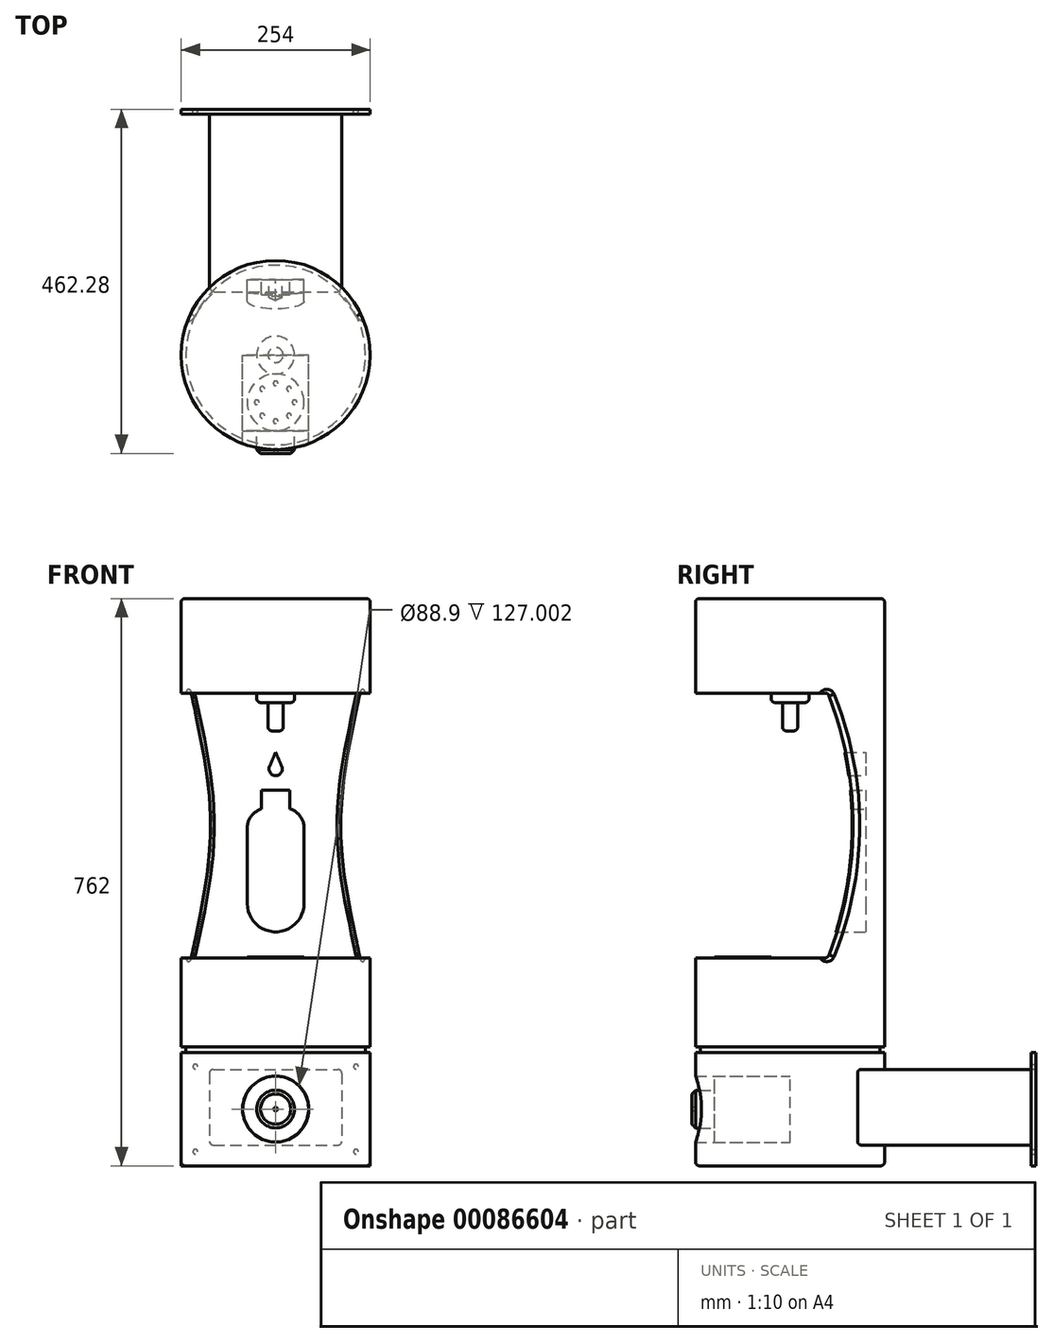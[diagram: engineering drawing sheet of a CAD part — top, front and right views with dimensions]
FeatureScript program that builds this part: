
annotation { "Feature Type Name" : "Feature", "Feature Type Description" : "" }
export const myFeature = defineFeature(function(context is Context, id is Id, definition is map)
    precondition{}
    {
        {
            var Q0;
            Q0=qCreatedBy(makeId("Top.planeOp"),FACE);
            var sketch = newSketch(context, id + "F0", { "sketchPlane" : qUnion([Q0])});
            skCircle(sketch, "E0", {"center": v(0, 0) * mm, "radius": 127 * mm});
            skSolve(sketch);
        }
        {
            var Q0;
            Q0=qCreatedBy(makeId("Front.planeOp"),FACE);
            cPlane(context, id + "F1", {"entities" : qUnion([Q0]), "cplaneType" : CPlaneType.OFFSET, "offset" : 101.6 * mm, "oppositeDirection" : true, "width" : 152.4 * mm, "height" : 152.4 * mm});
        }
        {
            var Q0;
            Q0 = qSketchRegion(id + "F0", true);
            extrude(context, id + "F2", {"entities" : qUnion([Q0]), "depth" : 762 * mm});
        }
        {
            var Q0;
            Q0=qCreatedBy(makeId("Right.planeOp"),FACE);
            var sketch = newSketch(context, id + "F3", { "sketchPlane" : qUnion([Q0])});
            skLineSegment(sketch, "E1.bottom", {"start": v(-152.4, 635) * mm, "end": v(50.8, 635) * mm});
            skLineSegment(sketch, "E1.top", {"start": v(-152.4, 279.4) * mm, "end": v(50.8, 279.4) * mm});
            skLineSegment(sketch, "E1.left", {"start": v(-152.4, 635) * mm, "end": v(-152.4, 279.4) * mm});
            skArc(sketch, "E2", {"start": v(50.8, 279.4) * mm, "mid": v(84.75, 457.2) * mm, "end": v(50.8, 635) * mm});
            skSolve(sketch);
        }
        {
            var Q0;
            Q0=qCreatedBy(id+"F1.planeOp",FACE);
            var sketch = newSketch(context, id + "F4", { "sketchPlane" : qUnion([Q0])});
            skLineSegment(sketch, "E3", {"start": v(0, 504.76) * mm, "end": v(-19.05, 504.76) * mm});
            skLineSegment(sketch, "E4", {"start": v(-19.05, 504.76) * mm, "end": v(-19.05, 479.36) * mm});
            skLineSegment(sketch, "E5", {"start": v(-38.1, 453.96) * mm, "end": v(-38.1, 352.36) * mm});
            skLineSegment(sketch, "E6", {"start": v(0, 96.81) * mm, "end": v(0, 607) * mm, "construction": true});
            skArc(sketch, "E7", {"start": v(-38.1, 453.96) * mm, "mid": v(-32.8, 469.83) * mm, "end": v(-19.05, 479.36) * mm});
            skArc(sketch, "E8", {"start": v(-38.1, 352.36) * mm, "mid": v(-26.94, 325.42) * mm, "end": v(0, 314.26) * mm});
            skLineSegment(sketch, "E9.MirrorCS", {"start": v(19.05, 504.76) * mm, "end": v(19.05, 479.36) * mm});
            skArc(sketch, "E10.MirrorCS", {"start": v(38.1, 352.36) * mm, "mid": v(26.94, 325.42) * mm, "end": v(0, 314.26) * mm});
            skLineSegment(sketch, "E11.MirrorCS", {"start": v(38.1, 453.96) * mm, "end": v(38.1, 352.36) * mm});
            skArc(sketch, "E12.MirrorCS", {"start": v(38.1, 453.96) * mm, "mid": v(32.8, 469.83) * mm, "end": v(19.05, 479.36) * mm});
            skLineSegment(sketch, "E13.MirrorCS", {"start": v(0, 504.76) * mm, "end": v(19.05, 504.76) * mm});
            skLineSegment(sketch, "E14", {"start": v(0, 555.56) * mm, "end": v(-8.17, 536.5) * mm});
            skArc(sketch, "E15", {"start": v(-8.17, 536.5) * mm, "mid": v(-7.42, 528.11) * mm, "end": v(0, 524.11) * mm});
            skArc(sketch, "E16.MirrorCS", {"start": v(8.17, 536.5) * mm, "mid": v(7.42, 528.11) * mm, "end": v(0, 524.11) * mm});
            skLineSegment(sketch, "E17.MirrorCS", {"start": v(0, 555.56) * mm, "end": v(8.17, 536.5) * mm});
            skSolve(sketch);
        }
        {
            var Q0;
            Q0 = qSketchRegion(id + "F3", true);
            extrude(context, id + "F5", {"entities" : qUnion([Q0]), "operationType" : NewBodyOperationType.REMOVE, "oppositeDirection" : true, "depth" : 152.4 * mm, "hasSecondDirection" : true, "secondDirectionOppositeDirection" : false, "secondDirectionDepth" : 152.4 * mm});
        }
        {
            var Q0;
            Q0=qCreatedBy(makeId("Front.planeOp"),FACE);
            var sketch = newSketch(context, id + "F6", { "sketchPlane" : qUnion([Q0])});
            skLineSegment(sketch, "E18.bottom", {"start": v(146.05, 160.02) * mm, "end": v(120.65, 160.02) * mm});
            skLineSegment(sketch, "E18.top", {"start": v(146.05, 152.4) * mm, "end": v(120.65, 152.4) * mm});
            skLineSegment(sketch, "E18.left", {"start": v(146.05, 160.02) * mm, "end": v(146.05, 152.4) * mm});
            skLineSegment(sketch, "E18.right", {"start": v(120.65, 160.02) * mm, "end": v(120.65, 152.4) * mm});
            skLineSegment(sketch, "E19", {"start": v(0, 0) * mm, "end": v(0, 233.9) * mm, "construction": true});
            skSolve(sketch);
        }
        {
            var Q0;
            Q0 = qSketchRegion(id + "F6", true);
            var Q1;
            Q1=sQuery(id+"F6.wireOp",EDGE,"E19");
            revolve(context, id + "F7", {"operationType" : NewBodyOperationType.REMOVE, "entities" : qUnion([Q0]), "axis" : qUnion([Q1]), "revolveType" : RevolveType.FULL, "oppositeDirection" : true});
        }
        {
            var Q0;
            Q0=qCreatedBy(makeId("Front.planeOp"),FACE);
            var sketch = newSketch(context, id + "F8", { "sketchPlane" : qUnion([Q0])});
            skLineSegment(sketch, "E20", {"start": v(0, 635) * mm, "end": v(0, 584.2) * mm});
            skLineSegment(sketch, "E21", {"start": v(0, 584.2) * mm, "end": v(10.16, 584.2) * mm});
            skLineSegment(sketch, "E22", {"start": v(10.16, 584.2) * mm, "end": v(10.16, 622.3) * mm});
            skLineSegment(sketch, "E23", {"start": v(10.16, 622.3) * mm, "end": v(25.4, 622.3) * mm});
            skLineSegment(sketch, "E24", {"start": v(25.4, 622.3) * mm, "end": v(25.4, 635) * mm});
            skLineSegment(sketch, "E25", {"start": v(0, 635) * mm, "end": v(25.4, 635) * mm});
            skLineSegment(sketch, "E26", {"start": v(0, 635) * mm, "end": v(0, 489.38) * mm, "construction": true});
            skSolve(sketch);
        }
        {
            var Q0;
            Q0 = qSketchRegion(id + "F8", true);
            var Q1;
            Q1=sQuery(id+"F8.wireOp",EDGE,"E26");
            revolve(context, id + "F9", {"entities" : qUnion([Q0]), "axis" : qUnion([Q1]), "revolveType" : RevolveType.FULL});
        }
        {
            var Q0;
            Q0=makeQuery(id+"F5.boolean.opBoolean","COPY",FACE,{"derivedFrom":makeQuery(id+"F5.opExtrude","SWEPT_FACE",FACE,{"disambiguationData":[OSD([sQuery(id+"F3.wireOp",EDGE,"E1.top")])]})});
            var sketch = newSketch(context, id + "F10", { "sketchPlane" : qUnion([Q0])});
            skCircle(sketch, "E27", {"center": v(0, -38.1) * mm, "radius": 3.18 * mm});
            skCircle(sketch, "E28.1.0", {"center": v(-17.96, -45.54) * mm, "radius": 3.18 * mm});
            skCircle(sketch, "E28.2.0", {"center": v(-25.4, -63.5) * mm, "radius": 3.18 * mm});
            skCircle(sketch, "E28.3.0", {"center": v(-17.96, -81.46) * mm, "radius": 3.18 * mm});
            skCircle(sketch, "E28.4.0", {"center": v(0, -88.9) * mm, "radius": 3.18 * mm});
            skCircle(sketch, "E28.5.0", {"center": v(17.96, -81.46) * mm, "radius": 3.18 * mm});
            skCircle(sketch, "E28.6.0", {"center": v(25.4, -63.5) * mm, "radius": 3.18 * mm});
            skCircle(sketch, "E28.7.0", {"center": v(17.96, -45.54) * mm, "radius": 3.18 * mm});
            skPoint(sketch, "E28.center", {"position": v(0, -63.5) * mm});
            skCircle(sketch, "E29.0", {"center": v(0, -63.5) * mm, "radius": 38.1 * mm});
            skSolve(sketch);
        }
        {
            var Q0;
            Q0 = qSketchRegion(id + "F10", true);
            extrude(context, id + "F11", {"entities" : qUnion([Q0]), "depth" : 1.27 * mm});
        }
        {
            var Q0;
            Q0=makeQuery(id+"F9.opRevolve","SWEPT_EDGE",EDGE,{"disambiguationData":[OSD([sQuery(id+"F8.wireOp",EDGE,"E23"),sQuery(id+"F8.wireOp",EDGE,"E24")])]});
            var Q1;
            Q1=makeQuery(id+"F9.opRevolve","SWEPT_EDGE",EDGE,{"disambiguationData":[OSD([sQuery(id+"F8.wireOp",EDGE,"E21"),sQuery(id+"F8.wireOp",EDGE,"E22")])]});
            fillet(context, id + "F12", {"entities" : qUnion([Q0, Q1]), "radius" : 5.08 * mm, "tangentPropagation" : true, "allowEdgeOverflow" : false});
        }
        {
            var Q0;
            Q0=makeQuery(id+"F5.boolean.opBoolean","COPY",FACE,{"derivedFrom":makeQuery(id+"F5.opExtrude","SWEPT_FACE",FACE,{"disambiguationData":[OSD([sQuery(id+"F3.wireOp",EDGE,"E2")])]})});
            var Q1;
            Q1=makeQuery(id+"F2.opExtrude","CAP_FACE",FACE,{"disambiguationData":[OSD([sQuery(id+"F0.wireOp",EDGE,"E0")])],"isStart":false});
            var Q2;
            Q2=makeQuery(id+"F2.opExtrude","CAP_FACE",FACE,{"disambiguationData":[OSD([sQuery(id+"F0.wireOp",EDGE,"E0")])],"isStart":true});
            fillet(context, id + "F13", {"entities" : qUnion([Q0, Q1, Q2]), "radius" : 5.08 * mm, "tangentPropagation" : true, "allowEdgeOverflow" : false});
        }
        {
            var Q0;
            Q0=qCreatedBy(makeId("Front.planeOp"),FACE);
            var sketch = newSketch(context, id + "F14", { "sketchPlane" : qUnion([Q0])});
            skLineSegment(sketch, "E30.bottom", {"start": v(-88.9, 129.54) * mm, "end": v(88.9, 129.54) * mm});
            skLineSegment(sketch, "E30.top", {"start": v(-88.9, 27.94) * mm, "end": v(88.9, 27.94) * mm});
            skLineSegment(sketch, "E30.left", {"start": v(-88.9, 129.54) * mm, "end": v(-88.9, 27.94) * mm});
            skLineSegment(sketch, "E30.right", {"start": v(88.9, 129.54) * mm, "end": v(88.9, 27.94) * mm});
            skLineSegment(sketch, "E31", {"start": v(-88.9, 78.74) * mm, "end": v(88.9, 78.74) * mm, "construction": true});
            skLineSegment(sketch, "E32", {"start": v(0, 0) * mm, "end": v(0, 109.7) * mm, "construction": true});
            skSolve(sketch);
        }
        {
            var Q0;
            Q0 = qSketchRegion(id + "F14", true);
            extrude(context, id + "F15", {"entities" : qUnion([Q0]), "operationType" : NewBodyOperationType.ADD, "oppositeDirection" : true, "depth" : 330.2 * mm});
        }
        {
            var Q0;
            Q0=makeQuery(id+"F15.opExtrude","CAP_FACE",FACE,{"disambiguationData":[OSD([sQuery(id+"F14.wireOp",EDGE,"E30.bottom"),sQuery(id+"F14.wireOp",EDGE,"E30.top"),sQuery(id+"F14.wireOp",EDGE,"E30.left"),sQuery(id+"F14.wireOp",EDGE,"E30.right")])],"isStart":false});
            var sketch = newSketch(context, id + "F16", { "sketchPlane" : qUnion([Q0])});
            skLineSegment(sketch, "E33.bottom", {"start": v(-127, 152.4) * mm, "end": v(127, 152.4) * mm});
            skLineSegment(sketch, "E33.top", {"start": v(-127, 0) * mm, "end": v(127, 0) * mm});
            skLineSegment(sketch, "E33.left", {"start": v(-127, 152.4) * mm, "end": v(-127, 0) * mm});
            skLineSegment(sketch, "E33.right", {"start": v(127, 152.4) * mm, "end": v(127, 0) * mm});
            skLineSegment(sketch, "E34", {"start": v(0, 0) * mm, "end": v(0, 100.7) * mm, "construction": true});
            skCircle(sketch, "E35", {"center": v(-107.95, 133.35) * mm, "radius": 3.18 * mm});
            skCircle(sketch, "E36", {"center": v(107.95, 133.35) * mm, "radius": 3.18 * mm});
            skCircle(sketch, "E37", {"center": v(107.95, 19.05) * mm, "radius": 3.18 * mm});
            skCircle(sketch, "E38", {"center": v(-107.95, 19.05) * mm, "radius": 3.18 * mm});
            skSolve(sketch);
        }
        {
            var Q0;
            Q0 = qSketchRegion(id + "F16", true);
            extrude(context, id + "F17", {"entities" : qUnion([Q0]), "operationType" : NewBodyOperationType.ADD, "oppositeDirection" : true, "depth" : 6.35 * mm});
        }
        {
            var Q0;
            Q0 = qSketchRegion(id + "F4", true);
            extrude(context, id + "F18", {"entities" : qUnion([Q0]), "depth" : 50.8 * mm});
        }
        {
            var Q0;
            Q0=qCreatedBy(makeId("Right.planeOp"),FACE);
            var sketch = newSketch(context, id + "F19", { "sketchPlane" : qUnion([Q0])});
            skArc(sketch, "E39.0", {"start": v(52.07, 282.64) * mm, "mid": v(84.75, 457.2) * mm, "end": v(52.07, 631.76) * mm});
            skArc(sketch, "E40.0", {"start": v(59.53, 307.27) * mm, "mid": v(82.87, 433.1) * mm, "end": v(72.23, 560.64) * mm});
            skLineSegment(sketch, "E41", {"start": v(72.23, 560.64) * mm, "end": v(34.13, 560.64) * mm});
            skLineSegment(sketch, "E42", {"start": v(34.13, 560.64) * mm, "end": v(34.13, 307.27) * mm});
            skLineSegment(sketch, "E43", {"start": v(34.13, 307.27) * mm, "end": v(59.53, 307.27) * mm});
            skSolve(sketch);
        }
        {
            var Q0;
            Q0 = qSketchRegion(id + "F19", true);
            extrude(context, id + "F20", {"entities" : qUnion([Q0]), "operationType" : NewBodyOperationType.REMOVE, "oppositeDirection" : true, "depth" : 101.6 * mm, "hasSecondDirection" : true, "secondDirectionOppositeDirection" : false, "secondDirectionDepth" : 101.6 * mm});
        }
        {
            var Q0;
            Q0=makeQuery(id+"F15.opExtrude","SWEPT_EDGE",EDGE,{"disambiguationData":[OSD([sQuery(id+"F14.wireOp",EDGE,"E30.bottom"),sQuery(id+"F14.wireOp",EDGE,"E30.right")])]});
            var Q1;
            Q1=makeQuery(id+"F15.opExtrude","SWEPT_EDGE",EDGE,{"disambiguationData":[OSD([sQuery(id+"F14.wireOp",EDGE,"E30.top"),sQuery(id+"F14.wireOp",EDGE,"E30.right")])]});
            var Q2;
            Q2=makeQuery(id+"F15.opExtrude","SWEPT_EDGE",EDGE,{"disambiguationData":[OSD([sQuery(id+"F14.wireOp",EDGE,"E30.top"),sQuery(id+"F14.wireOp",EDGE,"E30.left")])]});
            var Q3;
            Q3=makeQuery(id+"F15.opExtrude","SWEPT_EDGE",EDGE,{"disambiguationData":[OSD([sQuery(id+"F14.wireOp",EDGE,"E30.bottom"),sQuery(id+"F14.wireOp",EDGE,"E30.left")])]});
            fillet(context, id + "F21", {"entities" : qUnion([Q0, Q1, Q2, Q3]), "radius" : 5.08 * mm, "tangentPropagation" : true, "allowEdgeOverflow" : false});
        }
        {
            var Q0;
            Q0=qCreatedBy(makeId("Front.planeOp"),FACE);
            var sketch = newSketch(context, id + "F22", { "sketchPlane" : qUnion([Q0])});
            skCircle(sketch, "E44", {"center": v(0, 76.2) * mm, "radius": 44.45 * mm});
            skSolve(sketch);
        }
        {
            var Q0;
            Q0 = qSketchRegion(id + "F22", true);
            extrude(context, id + "F23", {"entities" : qUnion([Q0]), "operationType" : NewBodyOperationType.REMOVE, "depth" : 152.4 * mm});
        }
        {
            var Q0;
            Q0=makeQuery(id+"F23.boolean.opBoolean","COPY",FACE,{"derivedFrom":makeQuery(id+"F23.opExtrude","CAP_FACE",FACE,{"disambiguationData":[OSD([sQuery(id+"F22.wireOp",EDGE,"E44")])],"isStart":true})});
            extrude(context, id + "F24", {"entities" : qUnion([Q0]), "depth" : 101.6 * mm});
        }
        {
            var Q0;
            Q0=makeQuery(id+"F24.opExtrude","CAP_FACE",FACE,{"disambiguationData":[OSD([sQuery(id+"F22.wireOp",EDGE,"E44")])],"isStart":false});
            var sketch = newSketch(context, id + "F25", { "sketchPlane" : qUnion([Q0])});
            skCircle(sketch, "E45", {"center": v(0, 76.2) * mm, "radius": 25.4 * mm});
            skSolve(sketch);
        }
        {
            var Q0;
            Q0=makeQuery(id+"F25.imprint","IMPRINT",FACE,{"disambiguationData":[TD([[makeQuery(id+"F25.imprint","IMPRINT",EDGE,{"derivedFrom":sQuery(id+"F25.wireOp",EDGE,"E45")}),1.0]])]});
            extrude(context, id + "F26", {"entities" : qUnion([Q0]), "operationType" : NewBodyOperationType.ADD, "depth" : 30.48 * mm});
        }
        {
            var Q0;
            Q0=makeQuery(id+"F26.opExtrude","CAP_FACE",FACE,{"disambiguationData":[OSD([sQuery(id+"F25.wireOp",EDGE,"E45")])],"isStart":false});
            chamfer(context, id + "F27", {"entities" : qUnion([Q0]), "width" : 5.08 * mm, "tangentPropagation" : true});
        }
        {
            var Q0;
            Q0=makeQuery(id+"F26.opExtrude","CAP_FACE",FACE,{"disambiguationData":[OSD([sQuery(id+"F25.wireOp",EDGE,"E45")])],"isStart":false});
            var sketch = newSketch(context, id + "F28", { "sketchPlane" : qUnion([Q0])});
            skCircle(sketch, "E46", {"center": v(0, 76.2) * mm, "radius": 2.54 * mm});
            skSolve(sketch);
        }
        {
            var Q0;
            Q0 = qSketchRegion(id + "F28", true);
            extrude(context, id + "F29", {"entities" : qUnion([Q0]), "operationType" : NewBodyOperationType.REMOVE, "oppositeDirection" : true, "depth" : 6.35 * mm});
        }
    });
